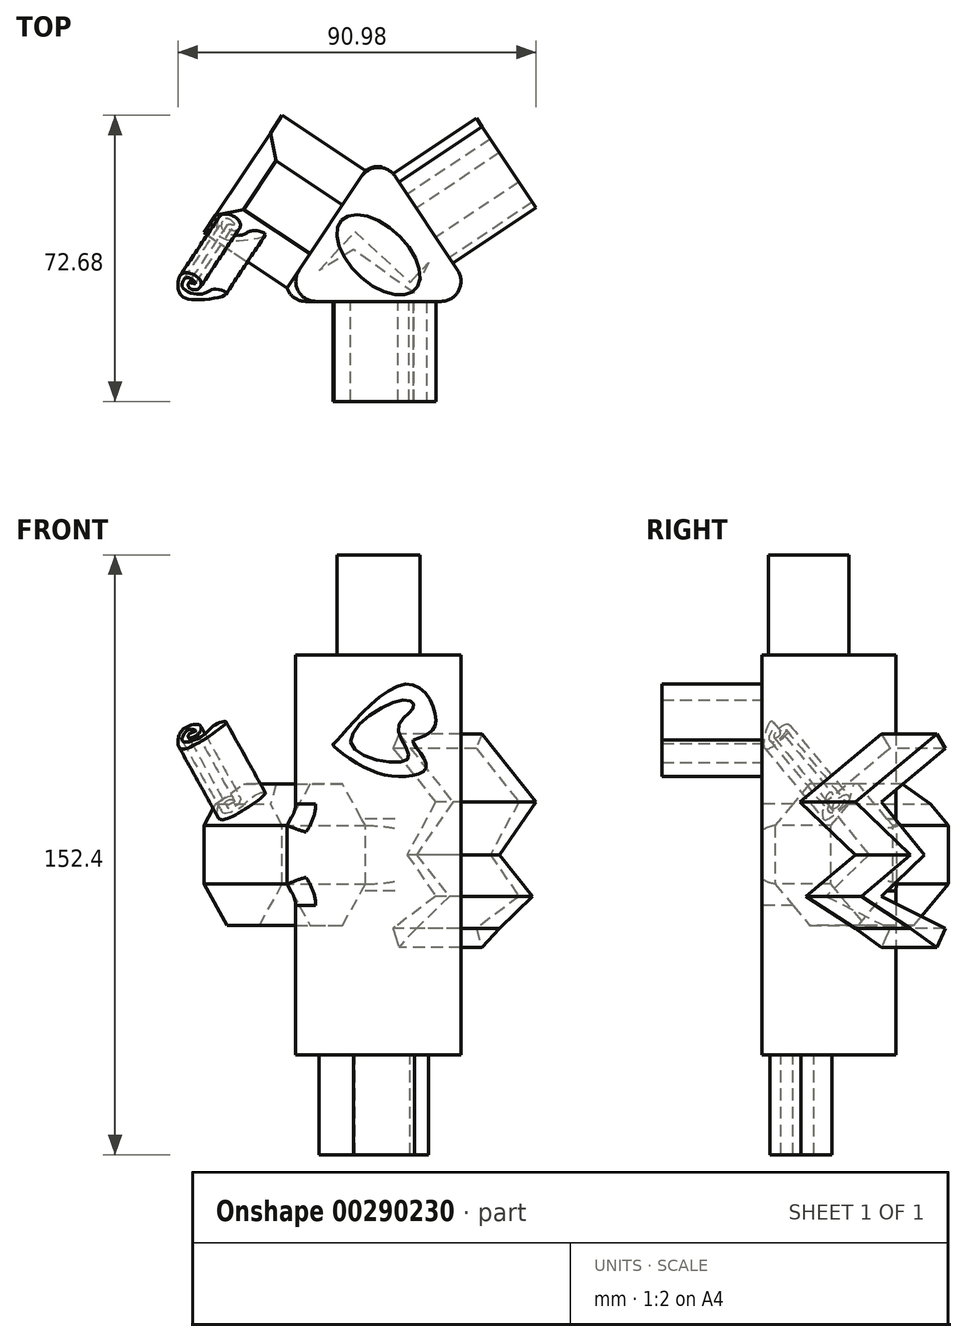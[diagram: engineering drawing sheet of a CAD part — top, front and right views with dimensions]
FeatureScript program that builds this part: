
annotation { "Feature Type Name" : "Feature", "Feature Type Description" : "" }
export const myFeature = defineFeature(function(context is Context, id is Id, definition is map)
    precondition{}
    {
        {
            var Q0;
            Q0=qCreatedBy(makeId("Top.planeOp"),FACE);
            var sketch = newSketch(context, id + "F0", { "sketchPlane" : qUnion([Q0])});
            skLineSegment(sketch, "E0", {"start": v(0, 0) * mm, "end": v(-25.4, -38.1) * mm});
            skLineSegment(sketch, "E1", {"start": v(-25.4, -38.1) * mm, "end": v(25.4, -38.1) * mm});
            skLineSegment(sketch, "E2", {"start": v(25.4, -38.1) * mm, "end": v(0, 0) * mm});
            skSolve(sketch);
        }
        {
            var Q0;
            Q0 = qSketchRegion(id + "F0", true);
            extrude(context, id + "F1", {"entities" : qUnion([Q0]), "endBound" : BoundingType.SYMMETRIC, "depth" : 101.6 * mm});
        }
        {
            var Q0;
            Q0=makeQuery(id+"F1.opExtrude","SWEPT_FACE",FACE,{"disambiguationData":[OSD([sQuery(id+"F0.wireOp",EDGE,"E0")])]});
            var sketch = newSketch(context, id + "F2", { "sketchPlane" : qUnion([Q0])});
            skCircle(sketch, "E3.cCircle", {"center": v(23.85, 0) * mm, "radius": 17.95 * mm, "construction": true});
            skLineSegment(sketch, "E3.0", {"start": v(5.9, -7.44) * mm, "end": v(5.9, 7.44) * mm});
            skLineSegment(sketch, "E3.1", {"start": v(5.9, 7.44) * mm, "end": v(16.42, 17.95) * mm});
            skLineSegment(sketch, "E3.2", {"start": v(16.42, 17.95) * mm, "end": v(31.29, 17.95) * mm});
            skLineSegment(sketch, "E3.3", {"start": v(31.29, 17.95) * mm, "end": v(41.8, 7.44) * mm});
            skLineSegment(sketch, "E3.4", {"start": v(41.8, 7.44) * mm, "end": v(41.8, -7.44) * mm});
            skLineSegment(sketch, "E3.5", {"start": v(41.8, -7.44) * mm, "end": v(31.29, -17.95) * mm});
            skLineSegment(sketch, "E3.6", {"start": v(31.29, -17.95) * mm, "end": v(16.42, -17.95) * mm});
            skLineSegment(sketch, "E3.7", {"start": v(16.42, -17.95) * mm, "end": v(5.9, -7.44) * mm});
            skPoint(sketch, "E3.0.midPoint", {"position": v(5.9, 0) * mm});
            skSolve(sketch);
        }
        {
            var Q0;
            Q0 = qSketchRegion(id + "F2", true);
            extrude(context, id + "F3", {"entities" : qUnion([Q0]), "operationType" : NewBodyOperationType.ADD, "depth" : 25.4 * mm});
        }
        {
            var Q0;
            Q0=makeQuery(id+"F1.opExtrude","CAP_FACE",FACE,{"disambiguationData":[OSD([sQuery(id+"F0.wireOp",EDGE,"E0"),sQuery(id+"F0.wireOp",EDGE,"E1"),sQuery(id+"F0.wireOp",EDGE,"E2")])],"isStart":false});
            var sketch = newSketch(context, id + "F4", { "sketchPlane" : qUnion([Q0])});
            skEllipse(sketch, "E4", {"center": v(0, -26.3) * mm, "majorRadius": 12.83 * mm, "minorRadius": 7.16 * mm, "majorAxis": v(-0.73, 0.68)});
            skSolve(sketch);
        }
        {
            var Q0;
            Q0 = qSketchRegion(id + "F4", true);
            extrude(context, id + "F5", {"entities" : qUnion([Q0]), "operationType" : NewBodyOperationType.ADD, "depth" : 25.4 * mm});
        }
        {
            var Q0;
            Q0=makeQuery(id+"F1.opExtrude","SWEPT_FACE",FACE,{"disambiguationData":[OSD([sQuery(id+"F0.wireOp",EDGE,"E2")])]});
            var sketch = newSketch(context, id + "F6", { "sketchPlane" : qUnion([Q0])});
            skLineSegment(sketch, "E5", {"start": v(-9.34, 30.74) * mm, "end": v(-34.16, 13.37) * mm});
            skLineSegment(sketch, "E6", {"start": v(-9.34, 30.74) * mm, "end": v(-6.74, 27.03) * mm});
            skLineSegment(sketch, "E7", {"start": v(-34.16, 13.37) * mm, "end": v(-17.36, 0) * mm});
            skLineSegment(sketch, "E8", {"start": v(-17.36, 0) * mm, "end": v(-32.47, -10.58) * mm});
            skLineSegment(sketch, "E9", {"start": v(-32.47, -10.58) * mm, "end": v(-17.36, -18.71) * mm});
            skLineSegment(sketch, "E10", {"start": v(-6.74, 27.03) * mm, "end": v(-26.25, 13.37) * mm});
            skLineSegment(sketch, "E11", {"start": v(-26.25, 13.37) * mm, "end": v(-13.16, 0) * mm});
            skLineSegment(sketch, "E12", {"start": v(-13.16, 0) * mm, "end": v(-26.25, -10.58) * mm});
            skLineSegment(sketch, "E13", {"start": v(-26.25, -10.58) * mm, "end": v(-6.74, -18.71) * mm});
            skLineSegment(sketch, "E14", {"start": v(-17.36, -18.71) * mm, "end": v(-9.34, -23.49) * mm});
            skLineSegment(sketch, "E15", {"start": v(-6.74, -18.71) * mm, "end": v(-9.34, -23.49) * mm});
            skSolve(sketch);
        }
        {
            var Q0;
            Q0 = qSketchRegion(id + "F6", true);
            extrude(context, id + "F7", {"entities" : qUnion([Q0]), "operationType" : NewBodyOperationType.ADD, "depth" : 25.4 * mm});
        }
        {
            var Q0;
            Q0=makeQuery(id+"F1.opExtrude","SWEPT_FACE",FACE,{"disambiguationData":[OSD([sQuery(id+"F0.wireOp",EDGE,"E1")])]});
            var sketch = newSketch(context, id + "F8", { "sketchPlane" : qUnion([Q0])});
            skFitSpline(sketch, "E16", {"points": [v(8.97, 29.22) * mm, v(14.51, 33.42) * mm, v(7.26, 43.35) * mm, v(-11.27, 28.26) * mm, v(-11.65, 28.07) * mm], "startDerivative": vector(33.74, 10.67) * mm, "endDerivative": vector(-4.14, 0.36) * mm});
            skFitSpline(sketch, "E17", {"points": [v(8.97, 29.22) * mm, v(8.97, 28.26) * mm, v(12.22, 22.53) * mm, v(6.5, 19.86) * mm, v(-4.77, 22.91) * mm, v(-11.57, 28.06) * mm, v(-11.27, 28.26) * mm], "startDerivative": vector(-4.28, -9.77) * mm, "endDerivative": vector(9.8, 2.36) * mm});
            skFitSpline(sketch, "E18", {"points": [v(6.32, 39.28) * mm, v(8.97, 37.53) * mm, v(5.05, 32.13) * mm, v(7.47, 24.3) * mm, v(-6.9, 28.06) * mm, v(6.32, 39.28) * mm]});
            skSolve(sketch);
        }
        {
            var Q0;
            Q0 = qSketchRegion(id + "F8", true);
            extrude(context, id + "F9", {"entities" : qUnion([Q0]), "operationType" : NewBodyOperationType.ADD, "depth" : 25.4 * mm});
        }
        {
            var Q0;
            Q0=makeQuery(id+"F1.opExtrude","CAP_FACE",FACE,{"disambiguationData":[OSD([sQuery(id+"F0.wireOp",EDGE,"E0"),sQuery(id+"F0.wireOp",EDGE,"E1"),sQuery(id+"F0.wireOp",EDGE,"E2")])],"isStart":true});
            var sketch = newSketch(context, id + "F10", { "sketchPlane" : qUnion([Q0])});
            skLineSegment(sketch, "E19", {"start": v(-15.09, 30.32) * mm, "end": v(-5.92, 20.39) * mm});
            skLineSegment(sketch, "E20", {"start": v(-5.92, 20.39) * mm, "end": v(8.07, 33.3) * mm});
            skLineSegment(sketch, "E21", {"start": v(8.07, 33.3) * mm, "end": v(12.76, 28.22) * mm});
            skLineSegment(sketch, "E22", {"start": v(12.76, 28.22) * mm, "end": v(9.17, 36.04) * mm});
            skLineSegment(sketch, "E23", {"start": v(9.17, 36.04) * mm, "end": v(-6.3, 24.97) * mm});
            skLineSegment(sketch, "E24", {"start": v(-6.3, 24.97) * mm, "end": v(-15.09, 30.32) * mm});
            skSolve(sketch);
        }
        {
            var Q0;
            Q0 = qSketchRegion(id + "F10", true);
            extrude(context, id + "F11", {"entities" : qUnion([Q0]), "operationType" : NewBodyOperationType.ADD, "depth" : 25.4 * mm});
        }
        {
            var Q0;
            Q0=makeQuery(id+"F3.opExtrude","SWEPT_FACE",FACE,{"disambiguationData":[OSD([sQuery(id+"F2.wireOp",EDGE,"E3.3")])]});
            var sketch = newSketch(context, id + "F12", { "sketchPlane" : qUnion([Q0])});
            skFitSpline(sketch, "E25", {"points": [v(-16.37, -6.19) * mm, v(-25.73, -11.3) * mm, v(-29.05, -10.61) * mm, v(-29.64, -7.3) * mm, v(-28.03, -3.21) * mm, v(-23.69, -3.9) * mm, v(-24.11, -7.3) * mm, v(-26.58, -7.55) * mm, v(-26.5, -6.02) * mm, v(-24.88, -5.68) * mm, v(-26.75, -4.32) * mm, v(-28.37, -8.15) * mm, v(-23.26, -8.66) * mm, v(-19.52, -5.85) * mm, v(-16.37, -6.19) * mm]});
            skSolve(sketch);
        }
        {
            var Q0;
            Q0 = qSketchRegion(id + "F12", true);
            extrude(context, id + "F13", {"entities" : qUnion([Q0]), "operationType" : NewBodyOperationType.ADD, "depth" : 25.4 * mm});
        }
        {
            var Q0;
            Q0=makeQuery(id+"F1.opExtrude","SWEPT_EDGE",EDGE,{"disambiguationData":[OSD([sQuery(id+"F0.wireOp",EDGE,"E1"),sQuery(id+"F0.wireOp",EDGE,"E2")])]});
            fillet(context, id + "F14", {"entities" : qUnion([Q0]), "radius" : 5.08 * mm, "tangentPropagation" : true, "allowEdgeOverflow" : false});
        }
        {
            var Q0;
            Q0=makeQuery(id+"F1.opExtrude","SWEPT_EDGE",EDGE,{"disambiguationData":[OSD([sQuery(id+"F0.wireOp",EDGE,"E0"),sQuery(id+"F0.wireOp",EDGE,"E2")])]});
            var Q1;
            Q1=makeQuery(id+"F1.opExtrude","SWEPT_EDGE",EDGE,{"disambiguationData":[OSD([sQuery(id+"F0.wireOp",EDGE,"E0"),sQuery(id+"F0.wireOp",EDGE,"E1")])]});
            fillet(context, id + "F15", {"entities" : qUnion([Q0, Q1]), "radius" : 5.08 * mm, "tangentPropagation" : true, "allowEdgeOverflow" : false});
        }
        {
            var Q0;
            Q0=makeQuery(id+"F3.opExtrude","CAP_EDGE",EDGE,{"disambiguationData":[OSD([sQuery(id+"F2.wireOp",EDGE,"E3.2")])],"isStart":false});
            chamfer(context, id + "F16", {"entities" : qUnion([Q0]), "width" : 5.08 * mm, "tangentPropagation" : true});
        }
    });
